# Revit family: ME_ST_WPB_Urbanfil_Tilemate_single_part_Access_Cover_ACO
name_source: partatom
category: Mechanical Equipment
units: mm (PartAtom-declared; Revit-internal decimal feet)

## family parameters
Always vertical = No
Cut with Voids When Loaded = No
Maintain Annotation Orientation = No
OmniClass Number = 23.35.50.27.11.11
OmniClass Title = Access Floors, Frames
Part Type = Normal
Room Calculation Point = No
Round Connector Dimension = Use Diameter
Shared = Yes
Work Plane-Based = Yes

## types (12) — shared parameters
Description = ACO Urbanfil-Tilemate (shallow pan access covers)
Export Type to IFC As = IfcBuildingElementProxy
IfcDescription = ACO Urbanfil-Tilemate (shallow pan access covers)
LOD = LOD 400
LOD300 = No
LOD400 = Yes
Manufacturer = ACO
Model = Urbanfil-Tilemate (shallow pan access covers)
Type Comments = -
Type IFC Predefined Type = USERDEFINED
URL = https://www.acoaccess.com.au
code_specification_URL_C_ANZRS = https://www.acoaccess.com.au
content_date_changed_C_ANZRS = 11-07-2025
content_version_C_ANZRS = 1.0
info_commercial_C_ANZRS = https://www.acoaccess.com.au
info_technical_C_ANZRS = https://www.acoaccess.com.au
installation_manual = https://www.acoaccess.com.au
instructions_for_use = https://www.acoaccess.com.au
lookuptable_name = urbanfil_tilemate
material_01_C_ANZRS = Steel, Galvanised
material_02_C_ANZRS = Concrete, Grey
material_C_ANZRS = Steel, Carbon
material_index = 1
productrange = Access Covers
region_index = 1
zero-valued in all types: Default Elevation

## per-type parameters (varying)
| type | type_index |
| Tilemate_TM24B_200x450 | 1 |
| Tilemate_TM33B_300x300 | 2 |
| Tilemate_TM36B_300x600 | 3 |
| Tilemate_TM365B_350x650 | 4 |
| Tilemate_TM44B_450x450 | 5 |
| Tilemate_TM46B_450x600 | 6 |
| Tilemate_TM66B_600x600 | 7 |
| Tilemate_TM67B_600x750 | 8 |
| Tilemate_TM69B_600x900 | 9 |
| Tilemate_TM77B_750x750 | 10 |
| Tilemate_TM94B_900x450 | 11 |
| Tilemate_TM99B_900x900 | 12 |

## geometry (parser evidence)
native form markers: Sweep x12
no freeform markers — native parametric forms only
